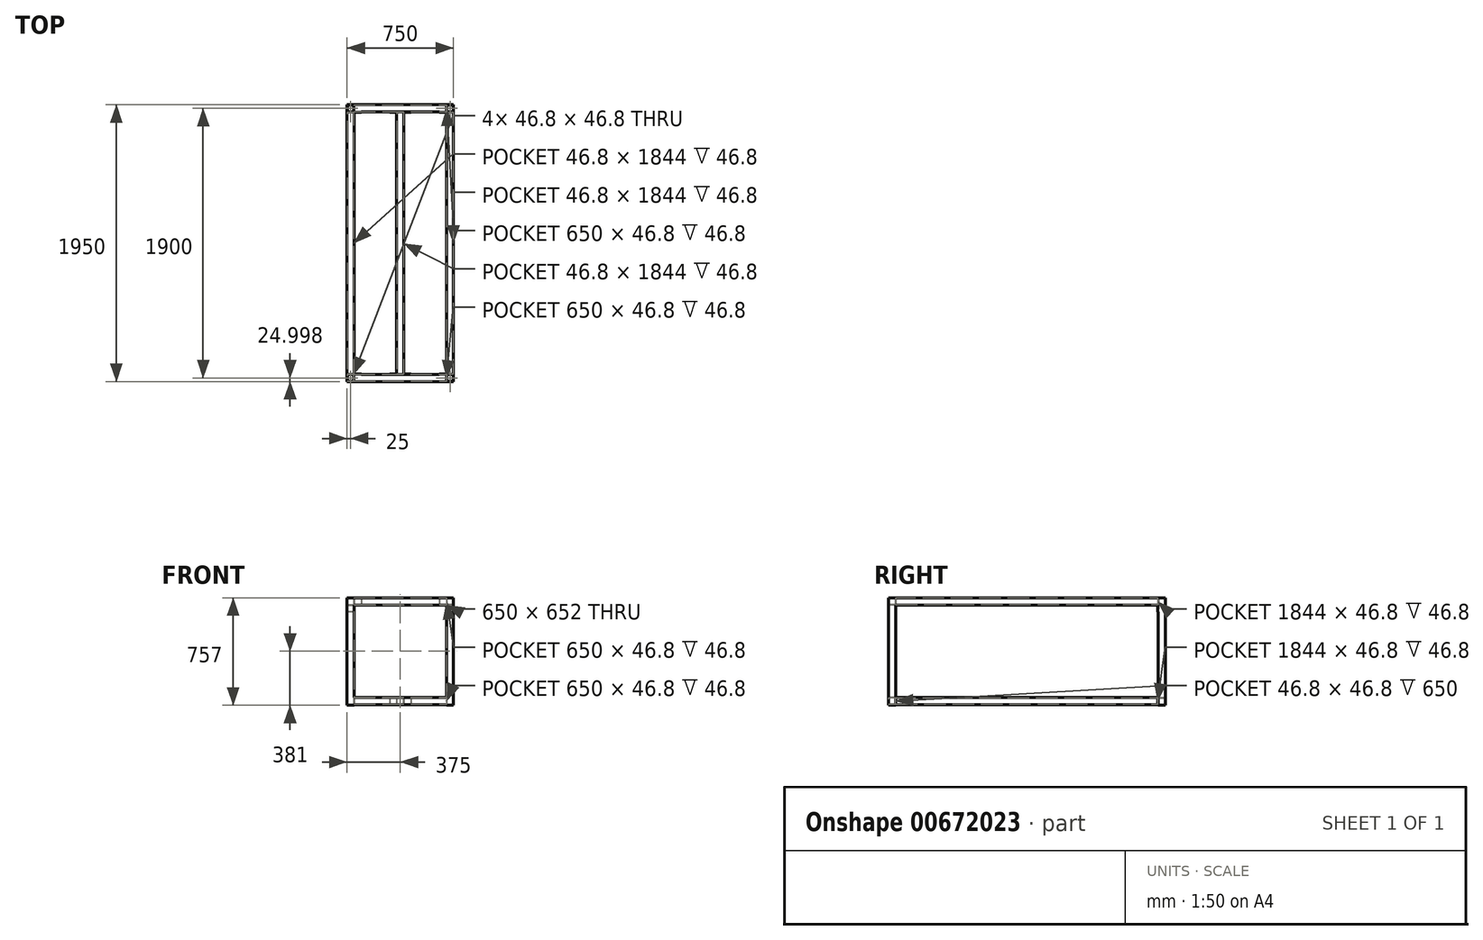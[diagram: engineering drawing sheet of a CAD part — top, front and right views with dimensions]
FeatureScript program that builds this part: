
annotation { "Feature Type Name" : "Feature", "Feature Type Description" : "" }
export const myFeature = defineFeature(function(context is Context, id is Id, definition is map)
    precondition{}
    {
        {
            var Q0;
            Q0=qCreatedBy(makeId("Top.planeOp"),FACE);
            var sketch = newSketch(context, id + "F0", { "sketchPlane" : qUnion([Q0])});
            skLineSegment(sketch, "E0.bottom", {"start": v(-50, 66.52) * mm, "end": v(0, 66.52) * mm});
            skLineSegment(sketch, "E0.top", {"start": v(-50, 16.52) * mm, "end": v(0, 16.52) * mm});
            skLineSegment(sketch, "E0.left", {"start": v(-50, 66.52) * mm, "end": v(-50, 16.52) * mm});
            skLineSegment(sketch, "E0.right", {"start": v(0, 66.52) * mm, "end": v(0, 16.52) * mm});
            skLineSegment(sketch, "E1.bottom", {"start": v(-48.4, 64.92) * mm, "end": v(-1.6, 64.92) * mm});
            skLineSegment(sketch, "E1.top", {"start": v(-48.4, 18.12) * mm, "end": v(-1.6, 18.12) * mm});
            skLineSegment(sketch, "E1.left", {"start": v(-48.4, 64.92) * mm, "end": v(-48.4, 18.12) * mm});
            skLineSegment(sketch, "E1.right", {"start": v(-1.6, 64.92) * mm, "end": v(-1.6, 18.12) * mm});
            skSolve(sketch);
        }
        {
            var Q0;
            Q0 = qSketchRegion(id + "F0", true);
            extrude(context, id + "F1", {"entities" : qUnion([Q0]), "depth" : 757 * mm, "offsetDistance" : 25 * mm});
        }
        {
            var Q0;
            Q0=makeQuery(id+"F1.opExtrude","SWEPT_FACE",FACE,{"disambiguationData":[OSD([sQuery(id+"F0.wireOp",EDGE,"E0.right")])]});
            var sketch = newSketch(context, id + "F2", { "sketchPlane" : qUnion([Q0])});
            skLineSegment(sketch, "E2.bottom", {"start": v(16.52, 757) * mm, "end": v(66.52, 757) * mm});
            skLineSegment(sketch, "E2.top", {"start": v(16.52, 707) * mm, "end": v(66.52, 707) * mm});
            skLineSegment(sketch, "E2.left", {"start": v(16.52, 757) * mm, "end": v(16.52, 707) * mm});
            skLineSegment(sketch, "E2.right", {"start": v(66.52, 757) * mm, "end": v(66.52, 707) * mm});
            skLineSegment(sketch, "E3.bottom", {"start": v(18.12, 755.4) * mm, "end": v(64.92, 755.4) * mm});
            skLineSegment(sketch, "E3.top", {"start": v(18.12, 708.6) * mm, "end": v(64.92, 708.6) * mm});
            skLineSegment(sketch, "E3.left", {"start": v(18.12, 755.4) * mm, "end": v(18.12, 708.6) * mm});
            skLineSegment(sketch, "E3.right", {"start": v(64.92, 755.4) * mm, "end": v(64.92, 708.6) * mm});
            skLineSegment(sketch, "E4.bottom", {"start": v(16.52, 55) * mm, "end": v(66.52, 55) * mm});
            skLineSegment(sketch, "E4.top", {"start": v(16.52, 5) * mm, "end": v(66.52, 5) * mm});
            skLineSegment(sketch, "E4.left", {"start": v(16.52, 55) * mm, "end": v(16.52, 5) * mm});
            skLineSegment(sketch, "E4.right", {"start": v(66.52, 55) * mm, "end": v(66.52, 5) * mm});
            skLineSegment(sketch, "E5.bottom", {"start": v(18.12, 53.4) * mm, "end": v(64.92, 53.4) * mm});
            skLineSegment(sketch, "E5.top", {"start": v(18.12, 6.6) * mm, "end": v(64.92, 6.6) * mm});
            skLineSegment(sketch, "E5.left", {"start": v(18.12, 53.4) * mm, "end": v(18.12, 6.6) * mm});
            skLineSegment(sketch, "E5.right", {"start": v(64.92, 53.4) * mm, "end": v(64.92, 6.6) * mm});
            skSolve(sketch);
        }
        {
            var Q0;
            Q0 = qSketchRegion(id + "F2", true);
            extrude(context, id + "F3", {"entities" : qUnion([Q0]), "operationType" : NewBodyOperationType.ADD, "depth" : 325 * mm, "offsetDistance" : 25 * mm});
        }
        {
            var Q0;
            Q0=makeQuery(id+"F3.boolean.opBoolean","MERGE",FACE,{"derivedFrom":[makeQuery(id+"F1.opExtrude","SWEPT_FACE",FACE,{"disambiguationData":[OSD([sQuery(id+"F0.wireOp",EDGE,"E0.top")])]}),makeQuery(id+"F3.opExtrude","SWEPT_FACE",FACE,{"disambiguationData":[OSD([sQuery(id+"F2.wireOp",EDGE,"E2.left")])]}),makeQuery(id+"F3.opExtrude","SWEPT_FACE",FACE,{"disambiguationData":[OSD([sQuery(id+"F2.wireOp",EDGE,"E4.left")])]})]});
            var sketch = newSketch(context, id + "F4", { "sketchPlane" : qUnion([Q0])});
            skLineSegment(sketch, "E6", {"start": v(-50, 757) * mm, "end": v(50, 757) * mm});
            skLineSegment(sketch, "E7", {"start": v(50, 757) * mm, "end": v(50, 707) * mm});
            skLineSegment(sketch, "E8", {"start": v(50, 707) * mm, "end": v(0, 707) * mm});
            skLineSegment(sketch, "E9", {"start": v(0, 707) * mm, "end": v(0, 657) * mm});
            skLineSegment(sketch, "E10", {"start": v(0, 657) * mm, "end": v(-50, 657) * mm});
            skLineSegment(sketch, "E11", {"start": v(-50, 657) * mm, "end": v(-50, 757) * mm});
            skLineSegment(sketch, "E12.bottom", {"start": v(325, 55) * mm, "end": v(250, 55) * mm});
            skLineSegment(sketch, "E12.top", {"start": v(325, 5) * mm, "end": v(250, 5) * mm});
            skLineSegment(sketch, "E12.left", {"start": v(325, 55) * mm, "end": v(325, 5) * mm});
            skLineSegment(sketch, "E12.right", {"start": v(250, 55) * mm, "end": v(250, 5) * mm});
            skSolve(sketch);
        }
        {
            var Q0;
            Q0 = qSketchRegion(id + "F4", true);
            extrude(context, id + "F5", {"entities" : qUnion([Q0]), "operationType" : NewBodyOperationType.ADD, "depth" : 3 * mm, "offsetDistance" : 25 * mm});
        }
        {
            var Q0;
            Q0=makeQuery(id+"F5.opExtrude","CAP_FACE",FACE,{"disambiguationData":[OSD([sQuery(id+"F4.wireOp",EDGE,"E6"),sQuery(id+"F4.wireOp",EDGE,"E7"),sQuery(id+"F4.wireOp",EDGE,"E8"),sQuery(id+"F4.wireOp",EDGE,"E9"),sQuery(id+"F4.wireOp",EDGE,"E10"),sQuery(id+"F4.wireOp",EDGE,"E11")])],"isStart":false});
            var sketch = newSketch(context, id + "F6", { "sketchPlane" : qUnion([Q0])});
            skLineSegment(sketch, "E13.bottom", {"start": v(-50, 757) * mm, "end": v(0, 757) * mm});
            skLineSegment(sketch, "E13.top", {"start": v(-50, 707) * mm, "end": v(0, 707) * mm});
            skLineSegment(sketch, "E13.left", {"start": v(-50, 757) * mm, "end": v(-50, 707) * mm});
            skLineSegment(sketch, "E13.right", {"start": v(0, 757) * mm, "end": v(0, 707) * mm});
            skLineSegment(sketch, "E14.bottom", {"start": v(-48.4, 755.4) * mm, "end": v(-1.6, 755.4) * mm});
            skLineSegment(sketch, "E14.top", {"start": v(-48.4, 708.6) * mm, "end": v(-1.6, 708.6) * mm});
            skLineSegment(sketch, "E14.left", {"start": v(-48.4, 755.4) * mm, "end": v(-48.4, 708.6) * mm});
            skLineSegment(sketch, "E14.right", {"start": v(-1.6, 755.4) * mm, "end": v(-1.6, 708.6) * mm});
            skSolve(sketch);
        }
        {
            var Q0;
            Q0 = qSketchRegion(id + "F6", true);
            extrude(context, id + "F7", {"entities" : qUnion([Q0]), "operationType" : NewBodyOperationType.ADD, "depth" : 922 * mm, "offsetDistance" : 25 * mm});
        }
        {
            var Q0;
            Q0=makeQuery(id+"F5.opExtrude","CAP_FACE",FACE,{"disambiguationData":[OSD([sQuery(id+"F4.wireOp",EDGE,"E12.bottom"),sQuery(id+"F4.wireOp",EDGE,"E12.top"),sQuery(id+"F4.wireOp",EDGE,"E12.left"),sQuery(id+"F4.wireOp",EDGE,"E12.right")])],"isStart":false});
            var sketch = newSketch(context, id + "F8", { "sketchPlane" : qUnion([Q0])});
            skLineSegment(sketch, "E15", {"start": v(325, 55) * mm, "end": v(300, 55) * mm});
            skLineSegment(sketch, "E16", {"start": v(300, 55) * mm, "end": v(300, 5) * mm});
            skLineSegment(sketch, "E17", {"start": v(300, 5) * mm, "end": v(325, 5) * mm});
            skLineSegment(sketch, "E18", {"start": v(325, 5) * mm, "end": v(325, 6.6) * mm});
            skLineSegment(sketch, "E19", {"start": v(325, 6.6) * mm, "end": v(301.6, 6.6) * mm});
            skLineSegment(sketch, "E20", {"start": v(301.6, 6.6) * mm, "end": v(301.6, 53.4) * mm});
            skLineSegment(sketch, "E21", {"start": v(301.6, 53.4) * mm, "end": v(325, 53.4) * mm});
            skLineSegment(sketch, "E22", {"start": v(325, 53.4) * mm, "end": v(325, 55) * mm});
            skSolve(sketch);
        }
        {
            var Q0;
            Q0 = qSketchRegion(id + "F8", true);
            extrude(context, id + "F9", {"entities" : qUnion([Q0]), "operationType" : NewBodyOperationType.ADD, "depth" : 922 * mm, "offsetDistance" : 25 * mm});
        }
        {
            var Q0;
            Q0=makeQuery(id+"F1.opExtrude","SWEPT_BODY",BODY,{"disambiguationData":[OSD([sQuery(id+"F0.wireOp",EDGE,"E0.bottom"),sQuery(id+"F0.wireOp",EDGE,"E0.top"),sQuery(id+"F0.wireOp",EDGE,"E0.left"),sQuery(id+"F0.wireOp",EDGE,"E0.right"),sQuery(id+"F0.wireOp",EDGE,"E1.bottom"),sQuery(id+"F0.wireOp",EDGE,"E1.top"),sQuery(id+"F0.wireOp",EDGE,"E1.left"),sQuery(id+"F0.wireOp",EDGE,"E1.right")])]});
            var Q1;
            Q1=makeQuery(id+"F9.boolean.opBoolean","MERGE",FACE,{"derivedFrom":[makeQuery(id+"F5.boolean.opBoolean","MERGE",FACE,{"derivedFrom":[makeQuery(id+"F3.opExtrude","CAP_FACE",FACE,{"disambiguationData":[OSD([sQuery(id+"F2.wireOp",EDGE,"E4.bottom"),sQuery(id+"F2.wireOp",EDGE,"E4.top"),sQuery(id+"F2.wireOp",EDGE,"E4.left"),sQuery(id+"F2.wireOp",EDGE,"E4.right"),sQuery(id+"F2.wireOp",EDGE,"E5.bottom"),sQuery(id+"F2.wireOp",EDGE,"E5.top"),sQuery(id+"F2.wireOp",EDGE,"E5.left"),sQuery(id+"F2.wireOp",EDGE,"E5.right")])],"isStart":false}),makeQuery(id+"F5.opExtrude","SWEPT_FACE",FACE,{"disambiguationData":[OSD([sQuery(id+"F4.wireOp",EDGE,"E12.left")])]})]}),makeQuery(id+"F9.opExtrude","SWEPT_FACE",FACE,{"disambiguationData":[OSD([sQuery(id+"F8.wireOp",EDGE,"E18")])]}),makeQuery(id+"F9.opExtrude","SWEPT_FACE",FACE,{"disambiguationData":[OSD([sQuery(id+"F8.wireOp",EDGE,"E22")])]})]});
            mirror(context, id + "F10", {"operationType" : NewBodyOperationType.ADD, "entities" : qUnion([Q0]), "mirrorPlane" : qUnion([Q1])});
        }
        {
            var Q0;
            Q0=makeQuery(id+"F1.opExtrude","SWEPT_BODY",BODY,{"disambiguationData":[OSD([sQuery(id+"F0.wireOp",EDGE,"E0.bottom"),sQuery(id+"F0.wireOp",EDGE,"E0.top"),sQuery(id+"F0.wireOp",EDGE,"E0.left"),sQuery(id+"F0.wireOp",EDGE,"E0.right"),sQuery(id+"F0.wireOp",EDGE,"E1.bottom"),sQuery(id+"F0.wireOp",EDGE,"E1.top"),sQuery(id+"F0.wireOp",EDGE,"E1.left"),sQuery(id+"F0.wireOp",EDGE,"E1.right")])]});
            var Q1;
            {var subQ0=makeQuery(id+"F9.opExtrude","CAP_FACE",FACE,{"disambiguationData":[OSD([sQuery(id+"F8.wireOp",EDGE,"E15"),sQuery(id+"F8.wireOp",EDGE,"E16"),sQuery(id+"F8.wireOp",EDGE,"E17"),sQuery(id+"F8.wireOp",EDGE,"E18"),sQuery(id+"F8.wireOp",EDGE,"E19"),sQuery(id+"F8.wireOp",EDGE,"E20"),sQuery(id+"F8.wireOp",EDGE,"E21"),sQuery(id+"F8.wireOp",EDGE,"E22")])],"isStart":false});Q1=makeQuery(id+"F10.boolean.opBoolean","MERGE",FACE,{"derivedFrom":[subQ0,makeQuery(id+"F10.opPattern","COPY",FACE,{"derivedFrom":subQ0,"instanceName":"1"})]});}
            mirror(context, id + "F11", {"operationType" : NewBodyOperationType.ADD, "entities" : qUnion([Q0]), "mirrorPlane" : qUnion([Q1])});
        }
    });
